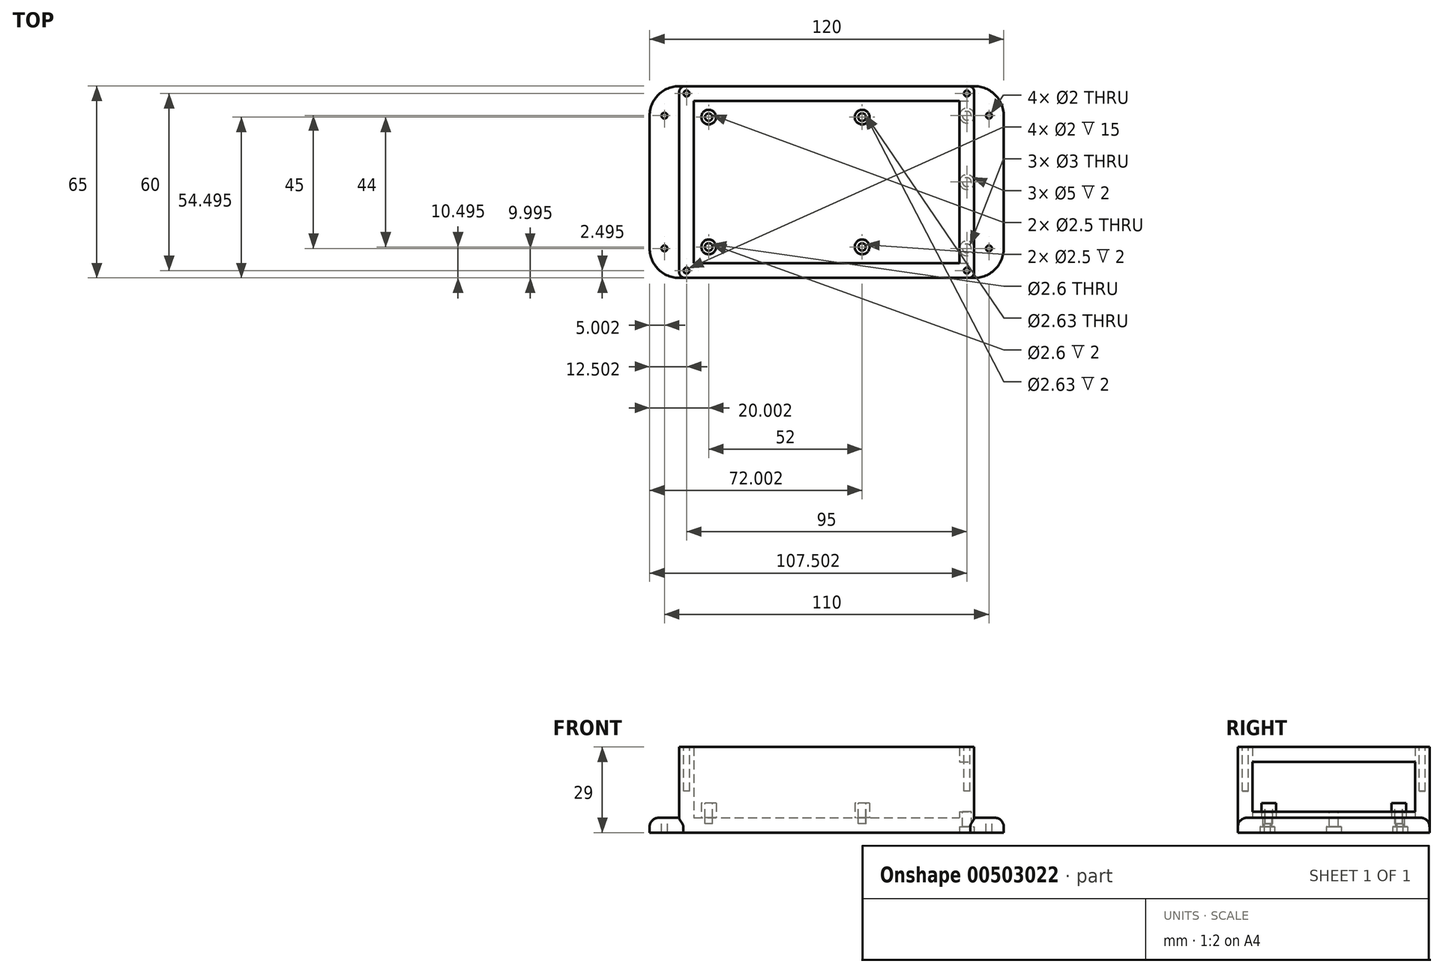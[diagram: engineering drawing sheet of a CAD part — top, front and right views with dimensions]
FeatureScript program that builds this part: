
annotation { "Feature Type Name" : "Feature", "Feature Type Description" : "" }
export const myFeature = defineFeature(function(context is Context, id is Id, definition is map)
    precondition{}
    {
        {
            var Q0;
            Q0=qCreatedBy(makeId("Top.planeOp"),FACE);
            var sketch = newSketch(context, id + "F0", { "sketchPlane" : qUnion([Q0])});
            skLineSegment(sketch, "E0.bottom", {"start": v(-47.53, 35.1) * mm, "end": v(72.47, 35.1) * mm});
            skLineSegment(sketch, "E0.top", {"start": v(-47.53, -29.9) * mm, "end": v(72.47, -29.9) * mm});
            skLineSegment(sketch, "E0.left", {"start": v(-47.53, 35.1) * mm, "end": v(-47.53, -29.9) * mm});
            skLineSegment(sketch, "E0.right", {"start": v(72.47, 35.1) * mm, "end": v(72.47, -29.9) * mm});
            skSolve(sketch);
        }
        {
            var Q0;
            Q0 = qSketchRegion(id + "F0", true);
            extrude(context, id + "F1", {"entities" : qUnion([Q0]), "depth" : 5 * mm});
        }
        {
            var Q0;
            Q0=makeQuery(id+"F1.opExtrude","CAP_FACE",FACE,{"disambiguationData":[OSD([sQuery(id+"F0.wireOp",EDGE,"E0.bottom"),sQuery(id+"F0.wireOp",EDGE,"E0.top"),sQuery(id+"F0.wireOp",EDGE,"E0.left"),sQuery(id+"F0.wireOp",EDGE,"E0.right")])],"isStart":false});
            var sketch = newSketch(context, id + "F2", { "sketchPlane" : qUnion([Q0])});
            skLineSegment(sketch, "E1.bottom", {"start": v(-37.53, 35.1) * mm, "end": v(62.47, 35.1) * mm});
            skLineSegment(sketch, "E1.top", {"start": v(-37.53, -29.9) * mm, "end": v(62.47, -29.9) * mm});
            skLineSegment(sketch, "E1.left", {"start": v(-37.53, 35.1) * mm, "end": v(-37.53, -29.9) * mm});
            skLineSegment(sketch, "E1.right", {"start": v(62.47, 35.1) * mm, "end": v(62.47, -29.9) * mm});
            skLineSegment(sketch, "E2.bottom", {"start": v(-32.53, 30.1) * mm, "end": v(57.47, 30.1) * mm});
            skLineSegment(sketch, "E2.top", {"start": v(-32.53, -24.9) * mm, "end": v(57.47, -24.9) * mm});
            skLineSegment(sketch, "E2.left", {"start": v(-32.53, 30.1) * mm, "end": v(-32.53, -24.9) * mm});
            skLineSegment(sketch, "E2.right", {"start": v(57.47, 30.1) * mm, "end": v(57.47, -24.9) * mm});
            skSolve(sketch);
        }
        {
            var Q0;
            Q0=makeQuery(id+"F2.imprint","IMPRINT",FACE,{"disambiguationData":[TD([[makeQuery(id+"F2.imprint","IMPRINT",EDGE,{"derivedFrom":sQuery(id+"F2.wireOp",EDGE,"E1.bottom")}),-1.0]])]});
            extrude(context, id + "F3", {"entities" : qUnion([Q0]), "operationType" : NewBodyOperationType.ADD, "depth" : 24 * mm});
        }
        {
            var Q0;
            Q0=makeQuery(id+"F1.opExtrude","SWEPT_EDGE",EDGE,{"disambiguationData":[OSD([sQuery(id+"F0.wireOp",EDGE,"E0.top"),sQuery(id+"F0.wireOp",EDGE,"E0.left")])]});
            var Q1;
            Q1=makeQuery(id+"F1.opExtrude","SWEPT_EDGE",EDGE,{"disambiguationData":[OSD([sQuery(id+"F0.wireOp",EDGE,"E0.bottom"),sQuery(id+"F0.wireOp",EDGE,"E0.left")])]});
            var Q2;
            Q2=makeQuery(id+"F1.opExtrude","SWEPT_EDGE",EDGE,{"disambiguationData":[OSD([sQuery(id+"F0.wireOp",EDGE,"E0.bottom"),sQuery(id+"F0.wireOp",EDGE,"E0.right")])]});
            var Q3;
            Q3=makeQuery(id+"F1.opExtrude","SWEPT_EDGE",EDGE,{"disambiguationData":[OSD([sQuery(id+"F0.wireOp",EDGE,"E0.top"),sQuery(id+"F0.wireOp",EDGE,"E0.right")])]});
            fillet(context, id + "F4", {"entities" : qUnion([Q0, Q1, Q2, Q3]), "radius" : 10 * mm, "tangentPropagation" : true, "allowEdgeOverflow" : false});
        }
        {
            var Q0;
            {var subQ0=sQuery(id+"F0.wireOp",EDGE,"E0.left");var subQ1=sQuery(id+"F0.wireOp",EDGE,"E0.top");var subQ2=sQuery(id+"F0.wireOp",EDGE,"E0.bottom");Q0=makeQuery(id+"F3.boolean.opBoolean","SPLIT",FACE,{"disambiguationData":[TD([makeQuery(id+"F1.opExtrude","SWEPT_FACE",FACE,{"disambiguationData":[OSD([subQ0])]})])],"derivedFrom":makeQuery(id+"F1.opExtrude","CAP_FACE",FACE,{"disambiguationData":[OSD([subQ2,subQ1,subQ0,sQuery(id+"F0.wireOp",EDGE,"E0.right")])],"isStart":false})});}
            var sketch = newSketch(context, id + "F5", { "sketchPlane" : qUnion([Q0])});
            skCircle(sketch, "E3", {"center": v(-42.53, 25.1) * mm, "radius": 1 * mm});
            skCircle(sketch, "E4", {"center": v(-42.53, -19.9) * mm, "radius": 1 * mm});
            skCircle(sketch, "E5", {"center": v(67.47, 25.1) * mm, "radius": 1 * mm});
            skCircle(sketch, "E6", {"center": v(67.47, -19.9) * mm, "radius": 1 * mm});
            skSolve(sketch);
        }
        {
            var Q0;
            Q0=makeQuery(id+"F5.imprint","IMPRINT",FACE,{"disambiguationData":[TD([[makeQuery(id+"F5.imprint","IMPRINT",EDGE,{"derivedFrom":sQuery(id+"F5.wireOp",EDGE,"E3")}),1.0]])]});
            var Q1;
            Q1=makeQuery(id+"F5.imprint","IMPRINT",FACE,{"disambiguationData":[TD([[makeQuery(id+"F5.imprint","IMPRINT",EDGE,{"derivedFrom":sQuery(id+"F5.wireOp",EDGE,"E4")}),1.0]])]});
            var Q2;
            Q2=makeQuery(id+"F5.imprint","IMPRINT",FACE,{"disambiguationData":[TD([[makeQuery(id+"F5.imprint","IMPRINT",EDGE,{"derivedFrom":sQuery(id+"F5.wireOp",EDGE,"E5")}),1.0]])]});
            var Q3;
            Q3=makeQuery(id+"F5.imprint","IMPRINT",FACE,{"disambiguationData":[TD([[makeQuery(id+"F5.imprint","IMPRINT",EDGE,{"derivedFrom":sQuery(id+"F5.wireOp",EDGE,"E6")}),1.0]])]});
            extrude(context, id + "F6", {"entities" : qUnion([Q0, Q1, Q2, Q3]), "operationType" : NewBodyOperationType.REMOVE, "oppositeDirection" : true, "depth" : 25 * mm});
        }
        {
            var Q0;
            Q0=makeQuery(id+"F3.opExtrude","CAP_FACE",FACE,{"disambiguationData":[OSD([sQuery(id+"F2.wireOp",EDGE,"E1.bottom"),sQuery(id+"F2.wireOp",EDGE,"E1.top"),sQuery(id+"F2.wireOp",EDGE,"E1.left"),sQuery(id+"F2.wireOp",EDGE,"E1.right"),sQuery(id+"F2.wireOp",EDGE,"E2.bottom"),sQuery(id+"F2.wireOp",EDGE,"E2.top"),sQuery(id+"F2.wireOp",EDGE,"E2.left"),sQuery(id+"F2.wireOp",EDGE,"E2.right")])],"isStart":false});
            var sketch = newSketch(context, id + "F7", { "sketchPlane" : qUnion([Q0])});
            skCircle(sketch, "E7", {"center": v(-35.03, 32.6) * mm, "radius": 1 * mm});
            skCircle(sketch, "E8", {"center": v(59.97, 32.6) * mm, "radius": 1 * mm});
            skCircle(sketch, "E9", {"center": v(-35.03, -27.4) * mm, "radius": 1 * mm});
            skCircle(sketch, "E10", {"center": v(59.97, -27.4) * mm, "radius": 1 * mm});
            skSolve(sketch);
        }
        {
            var Q0;
            Q0=makeQuery(id+"F7.imprint","IMPRINT",FACE,{"disambiguationData":[TD([[makeQuery(id+"F7.imprint","IMPRINT",EDGE,{"derivedFrom":sQuery(id+"F7.wireOp",EDGE,"E7")}),1.0]])]});
            var Q1;
            Q1=makeQuery(id+"F7.imprint","IMPRINT",FACE,{"disambiguationData":[TD([[makeQuery(id+"F7.imprint","IMPRINT",EDGE,{"derivedFrom":sQuery(id+"F7.wireOp",EDGE,"E9")}),1.0]])]});
            var Q2;
            Q2=makeQuery(id+"F7.imprint","IMPRINT",FACE,{"disambiguationData":[TD([[makeQuery(id+"F7.imprint","IMPRINT",EDGE,{"derivedFrom":sQuery(id+"F7.wireOp",EDGE,"E10")}),1.0]])]});
            var Q3;
            Q3=makeQuery(id+"F7.imprint","IMPRINT",FACE,{"disambiguationData":[TD([[makeQuery(id+"F7.imprint","IMPRINT",EDGE,{"derivedFrom":sQuery(id+"F7.wireOp",EDGE,"E8")}),1.0]])]});
            extrude(context, id + "F8", {"entities" : qUnion([Q0, Q1, Q2, Q3]), "operationType" : NewBodyOperationType.REMOVE, "oppositeDirection" : true, "depth" : 15 * mm});
        }
        {
            var Q0;
            Q0=makeQuery(id+"F3.opExtrude","SWEPT_FACE",FACE,{"disambiguationData":[OSD([sQuery(id+"F2.wireOp",EDGE,"E1.right")])]});
            var sketch = newSketch(context, id + "F9", { "sketchPlane" : qUnion([Q0])});
            skLineSegment(sketch, "E11.bottom", {"start": v(-24.9, 24) * mm, "end": v(30.1, 24) * mm});
            skLineSegment(sketch, "E11.top", {"start": v(-24.9, 7) * mm, "end": v(30.1, 7) * mm});
            skLineSegment(sketch, "E11.left", {"start": v(-24.9, 24) * mm, "end": v(-24.9, 7) * mm});
            skLineSegment(sketch, "E11.right", {"start": v(30.1, 24) * mm, "end": v(30.1, 7) * mm});
            skSolve(sketch);
        }
        {
            var Q0;
            Q0=makeQuery(id+"F9.imprint","IMPRINT",FACE,{"disambiguationData":[TD([[makeQuery(id+"F9.imprint","IMPRINT",EDGE,{"derivedFrom":sQuery(id+"F9.wireOp",EDGE,"E11.bottom")}),-1.0]])]});
            extrude(context, id + "F10", {"entities" : qUnion([Q0]), "operationType" : NewBodyOperationType.REMOVE, "oppositeDirection" : true, "depth" : 25 * mm});
        }
        {
            var Q0;
            {var subQ0=sQuery(id+"F0.wireOp",EDGE,"E0.top");var subQ1=sQuery(id+"F0.wireOp",EDGE,"E0.right");var subQ2=sQuery(id+"F0.wireOp",EDGE,"E0.bottom");Q0=makeQuery(id+"F4.opFillet","BLEND_EDGE",EDGE,{"blendedFrom":[makeQuery(id+"F1.opExtrude","SWEPT_EDGE",EDGE,{"disambiguationData":[OSD([subQ2,subQ1])]}),makeQuery(id+"F3.boolean.opBoolean","SPLIT",FACE,{"disambiguationData":[TD([makeQuery(id+"F1.opExtrude","SWEPT_FACE",FACE,{"disambiguationData":[OSD([subQ1])]})])],"derivedFrom":makeQuery(id+"F1.opExtrude","CAP_FACE",FACE,{"disambiguationData":[OSD([subQ2,subQ0,sQuery(id+"F0.wireOp",EDGE,"E0.left"),subQ1])],"isStart":false})})],"blendedInto":[makeQuery(id+"F3.boolean.opBoolean","SPLIT",FACE,{"disambiguationData":[TD([makeQuery(id+"F1.opExtrude","SWEPT_FACE",FACE,{"disambiguationData":[OSD([subQ1])]})])],"derivedFrom":makeQuery(id+"F1.opExtrude","CAP_FACE",FACE,{"disambiguationData":[OSD([subQ2,subQ0,sQuery(id+"F0.wireOp",EDGE,"E0.left"),subQ1])],"isStart":false})})]});}
            var Q1;
            {var subQ0=sQuery(id+"F0.wireOp",EDGE,"E0.left");var subQ1=sQuery(id+"F0.wireOp",EDGE,"E0.top");var subQ2=sQuery(id+"F0.wireOp",EDGE,"E0.bottom");Q1=makeQuery(id+"F4.opFillet","BLEND_EDGE",EDGE,{"blendedFrom":[makeQuery(id+"F1.opExtrude","SWEPT_EDGE",EDGE,{"disambiguationData":[OSD([subQ2,subQ0])]}),makeQuery(id+"F3.boolean.opBoolean","SPLIT",FACE,{"disambiguationData":[TD([makeQuery(id+"F1.opExtrude","SWEPT_FACE",FACE,{"disambiguationData":[OSD([subQ0])]})])],"derivedFrom":makeQuery(id+"F1.opExtrude","CAP_FACE",FACE,{"disambiguationData":[OSD([subQ2,subQ1,subQ0,sQuery(id+"F0.wireOp",EDGE,"E0.right")])],"isStart":false})})],"blendedInto":[makeQuery(id+"F3.boolean.opBoolean","SPLIT",FACE,{"disambiguationData":[TD([makeQuery(id+"F1.opExtrude","SWEPT_FACE",FACE,{"disambiguationData":[OSD([subQ0])]})])],"derivedFrom":makeQuery(id+"F1.opExtrude","CAP_FACE",FACE,{"disambiguationData":[OSD([subQ2,subQ1,subQ0,sQuery(id+"F0.wireOp",EDGE,"E0.right")])],"isStart":false})})]});}
            fillet(context, id + "F11", {"entities" : qUnion([Q0, Q1]), "radius" : 3 * mm, "tangentPropagation" : true, "allowEdgeOverflow" : false});
        }
        {
            var Q0;
            {var subQ0=sQuery(id+"F9.wireOp",EDGE,"E11.top");Q0=makeQuery(id+"F2Zl1YvZ3XMOMcV_1.boolean.opBoolean","MERGE",FACE,{"derivedFrom":[makeQuery(id+"F10.boolean.opBoolean","COPY",FACE,{"derivedFrom":makeQuery(id+"F10.opExtrude","SWEPT_FACE",FACE,{"disambiguationData":[OSD([subQ0])]})}),makeQuery(id+"F2Zl1YvZ3XMOMcV_1.opExtrude","SWEPT_FACE",FACE,{"disambiguationData":[OSD([sQuery(id+"F2.wireOp",EDGE,"E2.right"),subQ0])]})]});}
            var sketch = newSketch(context, id + "F12", { "sketchPlane" : qUnion([Q0])});
            skCircle(sketch, "E12", {"center": v(59.97, 25.1) * mm, "radius": 1.5 * mm});
            skCircle(sketch, "E13", {"center": v(59.97, -19.9) * mm, "radius": 1.5 * mm});
            skLineSegment(sketch, "E14", {"start": v(59.97, 25.1) * mm, "end": v(59.97, -19.9) * mm, "construction": true});
            skCircle(sketch, "E15", {"center": v(59.97, 2.6) * mm, "radius": 1.5 * mm});
            skSolve(sketch);
        }
        {
            var Q0;
            Q0=makeQuery(id+"F12.imprint","IMPRINT",FACE,{"disambiguationData":[TD([[makeQuery(id+"F12.imprint","IMPRINT",EDGE,{"derivedFrom":sQuery(id+"F12.wireOp",EDGE,"E13")}),1.0]])]});
            var Q1;
            Q1=makeQuery(id+"F12.imprint","IMPRINT",FACE,{"disambiguationData":[TD([[makeQuery(id+"F12.imprint","IMPRINT",EDGE,{"derivedFrom":sQuery(id+"F12.wireOp",EDGE,"E12")}),1.0]])]});
            var Q2;
            Q2=makeQuery(id+"F12.imprint","IMPRINT",FACE,{"disambiguationData":[TD([[makeQuery(id+"F12.imprint","IMPRINT",EDGE,{"derivedFrom":sQuery(id+"F12.wireOp",EDGE,"E15")}),1.0]])]});
            extrude(context, id + "F13", {"entities" : qUnion([Q0, Q1, Q2]), "operationType" : NewBodyOperationType.REMOVE, "oppositeDirection" : true, "depth" : 10 * mm});
        }
        {
            var Q0;
            Q0=makeQuery(id+"F3.boolean.opBoolean","SPLIT",FACE,{"disambiguationData":[TD([makeQuery(id+"F3.opExtrude","SWEPT_FACE",FACE,{"disambiguationData":[OSD([sQuery(id+"F2.wireOp",EDGE,"E2.bottom")])]})])],"derivedFrom":makeQuery(id+"F1.opExtrude","CAP_FACE",FACE,{"disambiguationData":[OSD([sQuery(id+"F0.wireOp",EDGE,"E0.bottom"),sQuery(id+"F0.wireOp",EDGE,"E0.top"),sQuery(id+"F0.wireOp",EDGE,"E0.left"),sQuery(id+"F0.wireOp",EDGE,"E0.right")])],"isStart":false})});
            var sketch = newSketch(context, id + "F14", { "sketchPlane" : qUnion([Q0])});
            skLineSegment(sketch, "E16", {"start": v(-27.53, 30.1) * mm, "end": v(-27.53, -24.9) * mm, "construction": true});
            skCircle(sketch, "E17", {"center": v(-27.53, -19.4) * mm, "radius": 2.5 * mm});
            skCircle(sketch, "E18", {"center": v(-27.53, 24.6) * mm, "radius": 2.5 * mm});
            skLineSegment(sketch, "E19", {"start": v(-27.53, 24.6) * mm, "end": v(57.47, 24.6) * mm, "construction": true});
            skLineSegment(sketch, "E20", {"start": v(-27.53, -19.4) * mm, "end": v(55.1, -19.4) * mm, "construction": true});
            skLineSegment(sketch, "E21", {"start": v(24.47, 24.6) * mm, "end": v(24.47, -19.4) * mm, "construction": true});
            skCircle(sketch, "E22", {"center": v(24.47, 24.6) * mm, "radius": 2.5 * mm});
            skCircle(sketch, "E23", {"center": v(24.47, -19.4) * mm, "radius": 2.5 * mm});
            skSolve(sketch);
        }
        {
            var Q0;
            Q0=makeQuery(id+"F14.imprint","IMPRINT",FACE,{"disambiguationData":[TD([[makeQuery(id+"F14.imprint","IMPRINT",EDGE,{"derivedFrom":sQuery(id+"F14.wireOp",EDGE,"E18")}),1.0]])]});
            var Q1;
            Q1=makeQuery(id+"F14.imprint","IMPRINT",FACE,{"disambiguationData":[TD([[makeQuery(id+"F14.imprint","IMPRINT",EDGE,{"derivedFrom":sQuery(id+"F14.wireOp",EDGE,"E17")}),1.0]])]});
            var Q2;
            Q2=makeQuery(id+"F14.imprint","IMPRINT",FACE,{"disambiguationData":[TD([[makeQuery(id+"F14.imprint","IMPRINT",EDGE,{"derivedFrom":sQuery(id+"F14.wireOp",EDGE,"E22")}),1.0]])]});
            var Q3;
            Q3=makeQuery(id+"F14.imprint","IMPRINT",FACE,{"disambiguationData":[TD([[makeQuery(id+"F14.imprint","IMPRINT",EDGE,{"derivedFrom":sQuery(id+"F14.wireOp",EDGE,"E23")}),1.0]])]});
            extrude(context, id + "F15", {"entities" : qUnion([Q0, Q1, Q2, Q3]), "depth" : 5 * mm});
        }
        {
            var Q0;
            Q0=makeQuery(id+"F15.opExtrude","CAP_FACE",FACE,{"disambiguationData":[OSD([sQuery(id+"F14.wireOp",EDGE,"E18")])],"isStart":false});
            var sketch = newSketch(context, id + "F16", { "sketchPlane" : qUnion([Q0])});
            skCircle(sketch, "E24", {"center": v(24.47, 24.6) * mm, "radius": 1.32 * mm});
            skCircle(sketch, "E25", {"center": v(24.47, -19.4) * mm, "radius": 1.25 * mm});
            skCircle(sketch, "E26", {"center": v(-27.53, -19.4) * mm, "radius": 1.3 * mm});
            skCircle(sketch, "E27", {"center": v(-27.53, 24.6) * mm, "radius": 1.25 * mm});
            skSolve(sketch);
        }
        {
            var Q0;
            Q0=makeQuery(id+"F16.imprint","IMPRINT",FACE,{"disambiguationData":[TD([[makeQuery(id+"F16.imprint","IMPRINT",EDGE,{"derivedFrom":sQuery(id+"F16.wireOp",EDGE,"E27")}),1.0]])]});
            var Q1;
            Q1=makeQuery(id+"F16.imprint","IMPRINT",FACE,{"disambiguationData":[TD([[makeQuery(id+"F16.imprint","IMPRINT",EDGE,{"derivedFrom":sQuery(id+"F16.wireOp",EDGE,"E24")}),1.0]])]});
            var Q2;
            Q2=makeQuery(id+"F16.imprint","IMPRINT",FACE,{"disambiguationData":[TD([[makeQuery(id+"F16.imprint","IMPRINT",EDGE,{"derivedFrom":sQuery(id+"F16.wireOp",EDGE,"E26")}),1.0]])]});
            var Q3;
            Q3=makeQuery(id+"F16.imprint","IMPRINT",FACE,{"disambiguationData":[TD([[makeQuery(id+"F16.imprint","IMPRINT",EDGE,{"derivedFrom":sQuery(id+"F16.wireOp",EDGE,"E25")}),1.0]])]});
            extrude(context, id + "F17", {"entities" : qUnion([Q0, Q1, Q2, Q3]), "operationType" : NewBodyOperationType.REMOVE, "oppositeDirection" : true, "depth" : 7 * mm});
        }
        {
            var Q0;
            Q0=makeQuery(id+"F3.opExtrude","SWEPT_EDGE",EDGE,{"disambiguationData":[OSD([sQuery(id+"F0.wireOp",EDGE,"E0.top"),sQuery(id+"F2.wireOp",EDGE,"E1.top"),sQuery(id+"F2.wireOp",EDGE,"E1.right")])]});
            var Q1;
            Q1=makeQuery(id+"F3.opExtrude","SWEPT_EDGE",EDGE,{"disambiguationData":[OSD([sQuery(id+"F0.wireOp",EDGE,"E0.top"),sQuery(id+"F2.wireOp",EDGE,"E1.top"),sQuery(id+"F2.wireOp",EDGE,"E1.left")])]});
            var Q2;
            Q2=makeQuery(id+"F3.opExtrude","SWEPT_EDGE",EDGE,{"disambiguationData":[OSD([sQuery(id+"F0.wireOp",EDGE,"E0.bottom"),sQuery(id+"F2.wireOp",EDGE,"E1.bottom"),sQuery(id+"F2.wireOp",EDGE,"E1.left")])]});
            var Q3;
            Q3=makeQuery(id+"F3.opExtrude","SWEPT_EDGE",EDGE,{"disambiguationData":[OSD([sQuery(id+"F0.wireOp",EDGE,"E0.bottom"),sQuery(id+"F2.wireOp",EDGE,"E1.bottom"),sQuery(id+"F2.wireOp",EDGE,"E1.right")])]});
            fillet(context, id + "F18", {"entities" : qUnion([Q0, Q1, Q2, Q3]), "radius" : 2 * mm, "tangentPropagation" : true, "allowEdgeOverflow" : false});
        }
        {
            var Q0;
            Q0=makeQuery(id+"F1.opExtrude","CAP_FACE",FACE,{"disambiguationData":[OSD([sQuery(id+"F0.wireOp",EDGE,"E0.bottom"),sQuery(id+"F0.wireOp",EDGE,"E0.top"),sQuery(id+"F0.wireOp",EDGE,"E0.left"),sQuery(id+"F0.wireOp",EDGE,"E0.right")])],"isStart":true});
            var sketch = newSketch(context, id + "F19", { "sketchPlane" : qUnion([Q0])});
            skLineSegment(sketch, "E28", {"start": v(59.97, 19.9) * mm, "end": v(59.97, -25.1) * mm, "construction": true});
            skCircle(sketch, "E29", {"center": v(59.97, 19.9) * mm, "radius": 2.5 * mm});
            skCircle(sketch, "E30", {"center": v(59.97, -2.6) * mm, "radius": 2.5 * mm});
            skCircle(sketch, "E31", {"center": v(59.97, -25.1) * mm, "radius": 2.5 * mm});
            skSolve(sketch);
        }
        {
            var Q0;
            Q0=makeQuery(id+"F19.imprint","IMPRINT",FACE,{"disambiguationData":[TD([[makeQuery(id+"F19.imprint","IMPRINT",EDGE,{"derivedFrom":sQuery(id+"F19.wireOp",EDGE,"E29")}),1.0]])]});
            var Q1;
            Q1=makeQuery(id+"F19.imprint","IMPRINT",FACE,{"disambiguationData":[TD([[makeQuery(id+"F19.imprint","IMPRINT",EDGE,{"derivedFrom":sQuery(id+"F19.wireOp",EDGE,"E30")}),1.0]])]});
            var Q2;
            Q2=makeQuery(id+"F19.imprint","IMPRINT",FACE,{"disambiguationData":[TD([[makeQuery(id+"F19.imprint","IMPRINT",EDGE,{"derivedFrom":sQuery(id+"F19.wireOp",EDGE,"E31")}),1.0]])]});
            extrude(context, id + "F20", {"entities" : qUnion([Q0, Q1, Q2]), "operationType" : NewBodyOperationType.REMOVE, "oppositeDirection" : true, "depth" : 2 * mm});
        }
    });
